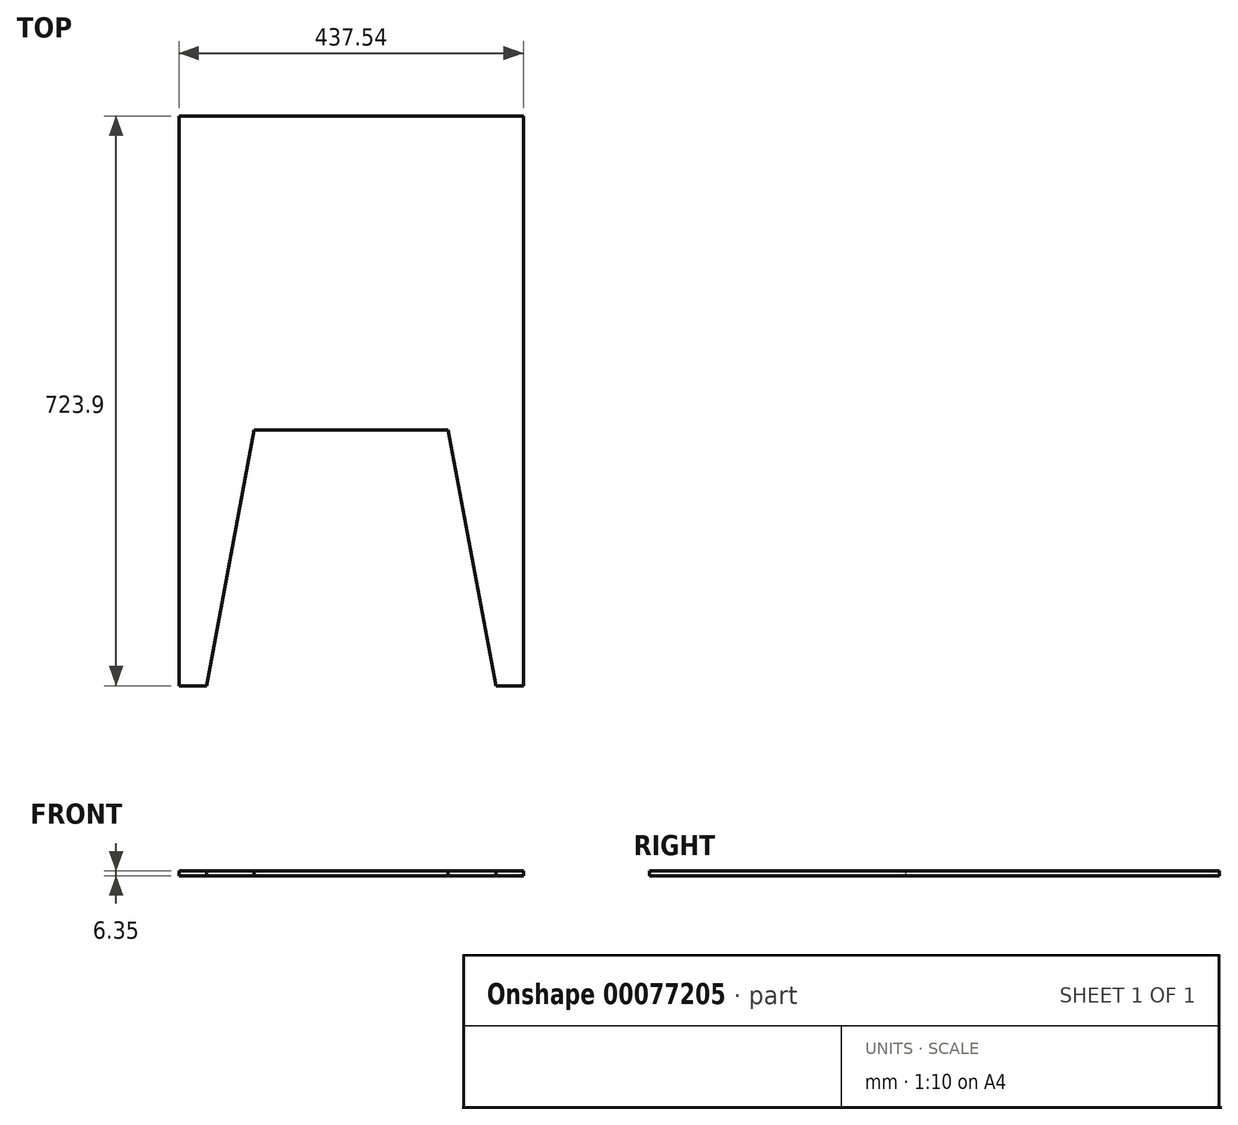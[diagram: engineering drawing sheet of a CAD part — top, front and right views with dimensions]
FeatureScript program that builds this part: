
annotation { "Feature Type Name" : "Feature", "Feature Type Description" : "" }
export const myFeature = defineFeature(function(context is Context, id is Id, definition is map)
    precondition{}
    {
        {
            var Q0;
            Q0=qCreatedBy(makeId("Top.planeOp"),FACE);
            var sketch = newSketch(context, id + "F0", { "sketchPlane" : qUnion([Q0])});
            skLineSegment(sketch, "E0", {"start": v(0, 0) * mm, "end": v(0, 723.9) * mm});
            skLineSegment(sketch, "E1", {"start": v(0, 723.9) * mm, "end": v(437.54, 723.9) * mm});
            skLineSegment(sketch, "E2", {"start": v(0, 0) * mm, "end": v(34.8, 0) * mm});
            skLineSegment(sketch, "E3", {"start": v(437.54, 723.9) * mm, "end": v(437.54, 0) * mm});
            skLineSegment(sketch, "E4", {"start": v(437.54, 0) * mm, "end": v(402.74, 0) * mm});
            skLineSegment(sketch, "E5", {"start": v(34.8, 0) * mm, "end": v(95.58, 325.25) * mm});
            skLineSegment(sketch, "E6", {"start": v(95.58, 325.25) * mm, "end": v(341.96, 325.25) * mm});
            skLineSegment(sketch, "E7", {"start": v(341.96, 325.25) * mm, "end": v(402.74, 0) * mm});
            skSolve(sketch);
        }
        {
            var Q0;
            Q0 = qSketchRegion(id + "F0", true);
            extrude(context, id + "F1", {"entities" : qUnion([Q0]), "depth" : 6.35 * mm});
        }
    });
